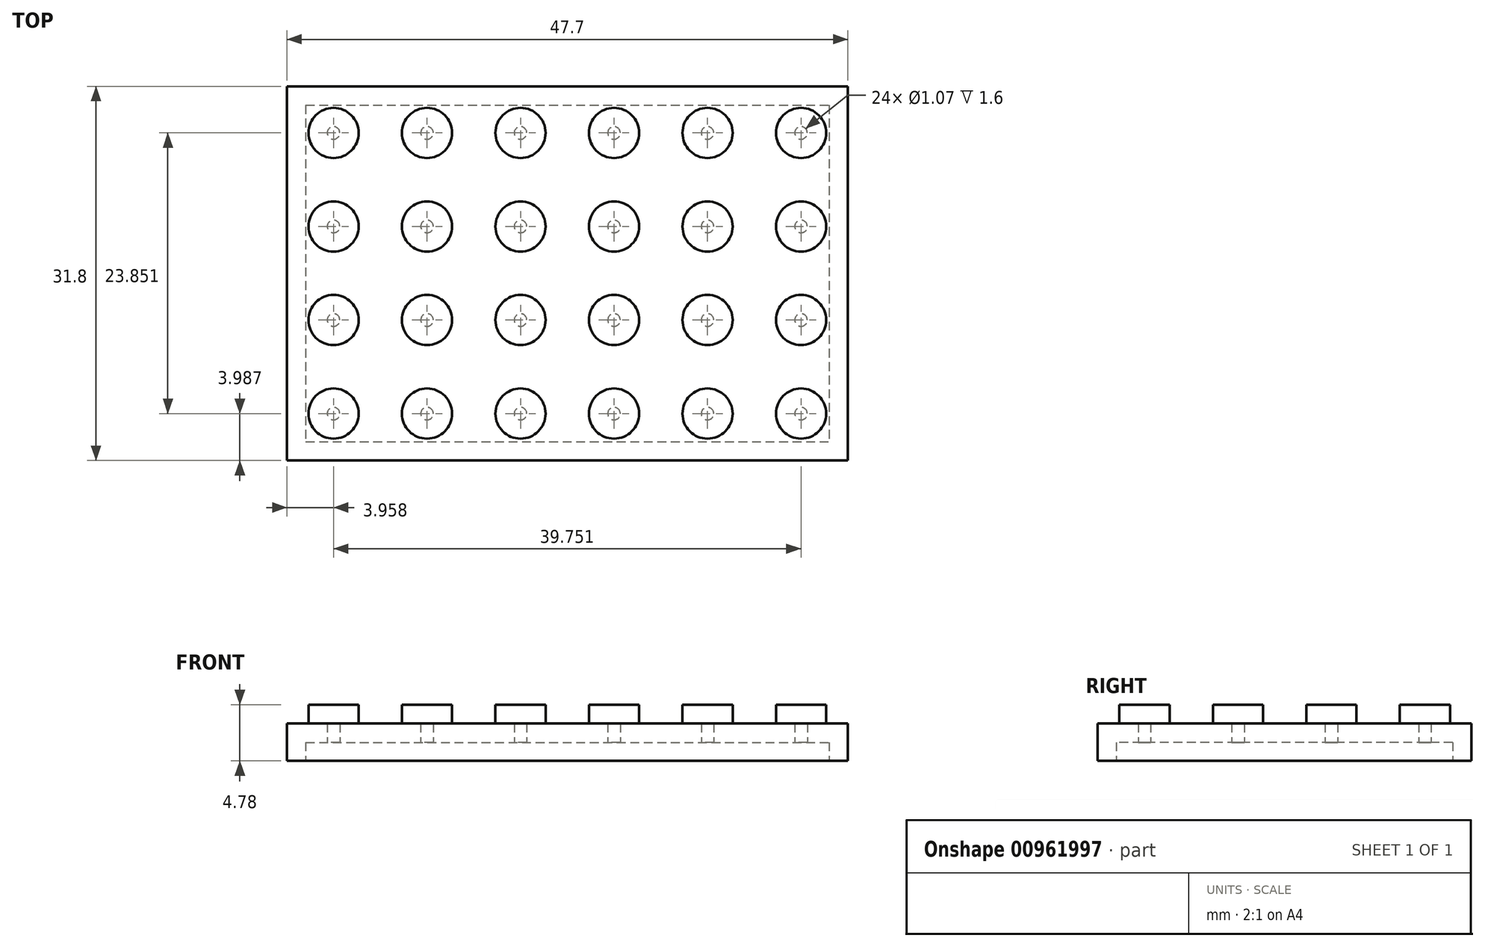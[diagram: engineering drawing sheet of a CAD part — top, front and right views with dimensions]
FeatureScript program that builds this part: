
annotation { "Feature Type Name" : "Feature", "Feature Type Description" : "" }
export const myFeature = defineFeature(function(context is Context, id is Id, definition is map)
    precondition{}
    {
        {
            var Q0;
            Q0=qCreatedBy(makeId("Top.planeOp"),FACE);
            var sketch = newSketch(context, id + "F0", { "sketchPlane" : qUnion([Q0])});
            skLineSegment(sketch, "E0.bottom", {"start": v(-28.22, 24.55) * mm, "end": v(19.48, 24.55) * mm});
            skLineSegment(sketch, "E0.top", {"start": v(-28.22, -7.25) * mm, "end": v(19.48, -7.25) * mm});
            skLineSegment(sketch, "E0.left", {"start": v(-28.22, 24.55) * mm, "end": v(-28.22, -7.25) * mm});
            skLineSegment(sketch, "E0.right", {"start": v(19.48, 24.55) * mm, "end": v(19.48, -7.25) * mm});
            skCircle(sketch, "E1", {"center": v(-24.26, 20.59) * mm, "radius": 2.13 * mm});
            skCircle(sketch, "E2.0.1.0", {"center": v(-24.26, 12.64) * mm, "radius": 2.13 * mm});
            skCircle(sketch, "E2.0.2.0", {"center": v(-24.26, 4.69) * mm, "radius": 2.13 * mm});
            skCircle(sketch, "E2.0.3.0", {"center": v(-24.26, -3.26) * mm, "radius": 2.13 * mm});
            skCircle(sketch, "E2.1.0.0", {"center": v(-16.31, 20.59) * mm, "radius": 2.13 * mm});
            skCircle(sketch, "E2.1.1.0", {"center": v(-16.31, 12.64) * mm, "radius": 2.13 * mm});
            skCircle(sketch, "E2.1.2.0", {"center": v(-16.31, 4.69) * mm, "radius": 2.13 * mm});
            skCircle(sketch, "E2.1.3.0", {"center": v(-16.31, -3.26) * mm, "radius": 2.13 * mm});
            skCircle(sketch, "E2.2.0.0", {"center": v(-8.36, 20.59) * mm, "radius": 2.13 * mm});
            skCircle(sketch, "E2.2.1.0", {"center": v(-8.36, 12.64) * mm, "radius": 2.13 * mm});
            skCircle(sketch, "E2.2.2.0", {"center": v(-8.36, 4.69) * mm, "radius": 2.13 * mm});
            skCircle(sketch, "E2.2.3.0", {"center": v(-8.36, -3.26) * mm, "radius": 2.13 * mm});
            skCircle(sketch, "E2.3.0.0", {"center": v(-0.41, 20.59) * mm, "radius": 2.13 * mm});
            skCircle(sketch, "E2.3.1.0", {"center": v(-0.41, 12.64) * mm, "radius": 2.13 * mm});
            skCircle(sketch, "E2.3.2.0", {"center": v(-0.41, 4.69) * mm, "radius": 2.13 * mm});
            skCircle(sketch, "E2.3.3.0", {"center": v(-0.41, -3.26) * mm, "radius": 2.13 * mm});
            skCircle(sketch, "E2.4.0.0", {"center": v(7.54, 20.59) * mm, "radius": 2.13 * mm});
            skCircle(sketch, "E2.4.1.0", {"center": v(7.54, 12.64) * mm, "radius": 2.13 * mm});
            skCircle(sketch, "E2.4.2.0", {"center": v(7.54, 4.69) * mm, "radius": 2.13 * mm});
            skCircle(sketch, "E2.4.3.0", {"center": v(7.54, -3.26) * mm, "radius": 2.13 * mm});
            skCircle(sketch, "E2.5.0.0", {"center": v(15.49, 20.59) * mm, "radius": 2.13 * mm});
            skCircle(sketch, "E2.5.1.0", {"center": v(15.49, 12.64) * mm, "radius": 2.13 * mm});
            skCircle(sketch, "E2.5.2.0", {"center": v(15.49, 4.69) * mm, "radius": 2.13 * mm});
            skCircle(sketch, "E2.5.3.0", {"center": v(15.49, -3.26) * mm, "radius": 2.13 * mm});
            skLineSegment(sketch, "E2.direction1", {"start": v(-24.26, 20.59) * mm, "end": v(-16.31, 20.59) * mm, "construction": true});
            skLineSegment(sketch, "E2.direction2", {"start": v(-24.26, 20.59) * mm, "end": v(-24.26, 12.64) * mm, "construction": true});
            skSolve(sketch);
        }
        {
            var Q0;
            Q0=makeQuery(id+"F0.imprint","IMPRINT",FACE,{"disambiguationData":[TD([[makeQuery(id+"F0.imprint","IMPRINT",EDGE,{"derivedFrom":sQuery(id+"F0.wireOp",EDGE,"E0.bottom")}),-1.0]])]});
            extrude(context, id + "F1", {"entities" : qUnion([Q0]), "depth" : 3.17 * mm, "offsetDistance" : 25.4 * mm});
        }
        {
            var Q0;
            Q0=makeQuery(id+"F0.imprint","IMPRINT",FACE,{"disambiguationData":[TD([[makeQuery(id+"F0.imprint","IMPRINT",EDGE,{"derivedFrom":sQuery(id+"F0.wireOp",EDGE,"E1")}),1.0]])]});
            var Q1;
            Q1=makeQuery(id+"F0.imprint","IMPRINT",FACE,{"disambiguationData":[TD([[makeQuery(id+"F0.imprint","IMPRINT",EDGE,{"derivedFrom":sQuery(id+"F0.wireOp",EDGE,"E2.1.0.0")}),1.0]])]});
            var Q2;
            Q2=makeQuery(id+"F0.imprint","IMPRINT",FACE,{"disambiguationData":[TD([[makeQuery(id+"F0.imprint","IMPRINT",EDGE,{"derivedFrom":sQuery(id+"F0.wireOp",EDGE,"E2.2.0.0")}),1.0]])]});
            var Q3;
            Q3=makeQuery(id+"F0.imprint","IMPRINT",FACE,{"disambiguationData":[TD([[makeQuery(id+"F0.imprint","IMPRINT",EDGE,{"derivedFrom":sQuery(id+"F0.wireOp",EDGE,"E2.3.0.0")}),1.0]])]});
            var Q4;
            Q4=makeQuery(id+"F0.imprint","IMPRINT",FACE,{"disambiguationData":[TD([[makeQuery(id+"F0.imprint","IMPRINT",EDGE,{"derivedFrom":sQuery(id+"F0.wireOp",EDGE,"E2.4.0.0")}),1.0]])]});
            var Q5;
            Q5=makeQuery(id+"F0.imprint","IMPRINT",FACE,{"disambiguationData":[TD([[makeQuery(id+"F0.imprint","IMPRINT",EDGE,{"derivedFrom":sQuery(id+"F0.wireOp",EDGE,"E2.5.0.0")}),1.0]])]});
            var Q6;
            Q6=makeQuery(id+"F0.imprint","IMPRINT",FACE,{"disambiguationData":[TD([[makeQuery(id+"F0.imprint","IMPRINT",EDGE,{"derivedFrom":sQuery(id+"F0.wireOp",EDGE,"E2.5.1.0")}),1.0]])]});
            var Q7;
            Q7=makeQuery(id+"F0.imprint","IMPRINT",FACE,{"disambiguationData":[TD([[makeQuery(id+"F0.imprint","IMPRINT",EDGE,{"derivedFrom":sQuery(id+"F0.wireOp",EDGE,"E2.4.1.0")}),1.0]])]});
            var Q8;
            Q8=makeQuery(id+"F0.imprint","IMPRINT",FACE,{"disambiguationData":[TD([[makeQuery(id+"F0.imprint","IMPRINT",EDGE,{"derivedFrom":sQuery(id+"F0.wireOp",EDGE,"E2.3.1.0")}),1.0]])]});
            var Q9;
            Q9=makeQuery(id+"F0.imprint","IMPRINT",FACE,{"disambiguationData":[TD([[makeQuery(id+"F0.imprint","IMPRINT",EDGE,{"derivedFrom":sQuery(id+"F0.wireOp",EDGE,"E2.2.1.0")}),1.0]])]});
            var Q10;
            Q10=makeQuery(id+"F0.imprint","IMPRINT",FACE,{"disambiguationData":[TD([[makeQuery(id+"F0.imprint","IMPRINT",EDGE,{"derivedFrom":sQuery(id+"F0.wireOp",EDGE,"E2.1.1.0")}),1.0]])]});
            var Q11;
            Q11=makeQuery(id+"F0.imprint","IMPRINT",FACE,{"disambiguationData":[TD([[makeQuery(id+"F0.imprint","IMPRINT",EDGE,{"derivedFrom":sQuery(id+"F0.wireOp",EDGE,"E2.0.1.0")}),1.0]])]});
            var Q12;
            Q12=makeQuery(id+"F0.imprint","IMPRINT",FACE,{"disambiguationData":[TD([[makeQuery(id+"F0.imprint","IMPRINT",EDGE,{"derivedFrom":sQuery(id+"F0.wireOp",EDGE,"E2.0.2.0")}),1.0]])]});
            var Q13;
            Q13=makeQuery(id+"F0.imprint","IMPRINT",FACE,{"disambiguationData":[TD([[makeQuery(id+"F0.imprint","IMPRINT",EDGE,{"derivedFrom":sQuery(id+"F0.wireOp",EDGE,"E2.1.2.0")}),1.0]])]});
            var Q14;
            Q14=makeQuery(id+"F0.imprint","IMPRINT",FACE,{"disambiguationData":[TD([[makeQuery(id+"F0.imprint","IMPRINT",EDGE,{"derivedFrom":sQuery(id+"F0.wireOp",EDGE,"E2.2.2.0")}),1.0]])]});
            var Q15;
            Q15=makeQuery(id+"F0.imprint","IMPRINT",FACE,{"disambiguationData":[TD([[makeQuery(id+"F0.imprint","IMPRINT",EDGE,{"derivedFrom":sQuery(id+"F0.wireOp",EDGE,"E2.3.2.0")}),1.0]])]});
            var Q16;
            Q16=makeQuery(id+"F0.imprint","IMPRINT",FACE,{"disambiguationData":[TD([[makeQuery(id+"F0.imprint","IMPRINT",EDGE,{"derivedFrom":sQuery(id+"F0.wireOp",EDGE,"E2.4.2.0")}),1.0]])]});
            var Q17;
            Q17=makeQuery(id+"F0.imprint","IMPRINT",FACE,{"disambiguationData":[TD([[makeQuery(id+"F0.imprint","IMPRINT",EDGE,{"derivedFrom":sQuery(id+"F0.wireOp",EDGE,"E2.5.2.0")}),1.0]])]});
            var Q18;
            Q18=makeQuery(id+"F0.imprint","IMPRINT",FACE,{"disambiguationData":[TD([[makeQuery(id+"F0.imprint","IMPRINT",EDGE,{"derivedFrom":sQuery(id+"F0.wireOp",EDGE,"E2.5.3.0")}),1.0]])]});
            var Q19;
            Q19=makeQuery(id+"F0.imprint","IMPRINT",FACE,{"disambiguationData":[TD([[makeQuery(id+"F0.imprint","IMPRINT",EDGE,{"derivedFrom":sQuery(id+"F0.wireOp",EDGE,"E2.4.3.0")}),1.0]])]});
            var Q20;
            Q20=makeQuery(id+"F0.imprint","IMPRINT",FACE,{"disambiguationData":[TD([[makeQuery(id+"F0.imprint","IMPRINT",EDGE,{"derivedFrom":sQuery(id+"F0.wireOp",EDGE,"E2.3.3.0")}),1.0]])]});
            var Q21;
            Q21=makeQuery(id+"F0.imprint","IMPRINT",FACE,{"disambiguationData":[TD([[makeQuery(id+"F0.imprint","IMPRINT",EDGE,{"derivedFrom":sQuery(id+"F0.wireOp",EDGE,"E2.2.3.0")}),1.0]])]});
            var Q22;
            Q22=makeQuery(id+"F0.imprint","IMPRINT",FACE,{"disambiguationData":[TD([[makeQuery(id+"F0.imprint","IMPRINT",EDGE,{"derivedFrom":sQuery(id+"F0.wireOp",EDGE,"E2.1.3.0")}),1.0]])]});
            var Q23;
            Q23=makeQuery(id+"F0.imprint","IMPRINT",FACE,{"disambiguationData":[TD([[makeQuery(id+"F0.imprint","IMPRINT",EDGE,{"derivedFrom":sQuery(id+"F0.wireOp",EDGE,"E2.0.3.0")}),1.0]])]});
            extrude(context, id + "F2", {"entities" : qUnion([Q0, Q1, Q2, Q3, Q4, Q5, Q6, Q7, Q8, Q9, Q10, Q11, Q12, Q13, Q14, Q15, Q16, Q17, Q18, Q19, Q20, Q21, Q22, Q23]), "operationType" : NewBodyOperationType.ADD, "depth" : 4.78 * mm, "offsetDistance" : 25.4 * mm});
        }
        {
            var Q0;
            {var subQ0=sQuery(id+"F0.wireOp",EDGE,"E2.5.3.0");var subQ1=sQuery(id+"F0.wireOp",EDGE,"E2.5.2.0");var subQ2=sQuery(id+"F0.wireOp",EDGE,"E2.5.1.0");var subQ3=sQuery(id+"F0.wireOp",EDGE,"E2.5.0.0");var subQ4=sQuery(id+"F0.wireOp",EDGE,"E2.4.3.0");var subQ5=sQuery(id+"F0.wireOp",EDGE,"E2.4.2.0");var subQ6=sQuery(id+"F0.wireOp",EDGE,"E2.4.1.0");var subQ7=sQuery(id+"F0.wireOp",EDGE,"E2.4.0.0");var subQ8=sQuery(id+"F0.wireOp",EDGE,"E2.3.3.0");var subQ9=sQuery(id+"F0.wireOp",EDGE,"E2.3.2.0");var subQ10=sQuery(id+"F0.wireOp",EDGE,"E2.3.1.0");var subQ11=sQuery(id+"F0.wireOp",EDGE,"E2.3.0.0");var subQ12=sQuery(id+"F0.wireOp",EDGE,"E2.2.3.0");var subQ13=sQuery(id+"F0.wireOp",EDGE,"E2.2.2.0");var subQ14=sQuery(id+"F0.wireOp",EDGE,"E2.2.1.0");var subQ15=sQuery(id+"F0.wireOp",EDGE,"E2.2.0.0");var subQ16=sQuery(id+"F0.wireOp",EDGE,"E2.1.3.0");var subQ17=sQuery(id+"F0.wireOp",EDGE,"E2.1.2.0");var subQ18=sQuery(id+"F0.wireOp",EDGE,"E2.1.1.0");var subQ19=sQuery(id+"F0.wireOp",EDGE,"E2.1.0.0");var subQ20=sQuery(id+"F0.wireOp",EDGE,"E2.0.3.0");var subQ21=sQuery(id+"F0.wireOp",EDGE,"E2.0.2.0");var subQ22=sQuery(id+"F0.wireOp",EDGE,"E2.0.1.0");var subQ23=sQuery(id+"F0.wireOp",EDGE,"E1");Q0=makeQuery(id+"F2.boolean.opBoolean","MERGE",FACE,{"derivedFrom":[makeQuery(id+"F1.opExtrude","CAP_FACE",FACE,{"disambiguationData":[OSD([sQuery(id+"F0.wireOp",EDGE,"E0.bottom"),sQuery(id+"F0.wireOp",EDGE,"E0.top"),sQuery(id+"F0.wireOp",EDGE,"E0.left"),sQuery(id+"F0.wireOp",EDGE,"E0.right"),subQ23,subQ22,subQ21,subQ20,subQ19,subQ18,subQ17,subQ16,subQ15,subQ14,subQ13,subQ12,subQ11,subQ10,subQ9,subQ8,subQ7,subQ6,subQ5,subQ4,subQ3,subQ2,subQ1,subQ0])],"isStart":true}),makeQuery(id+"F2.opExtrude","CAP_FACE",FACE,{"disambiguationData":[OSD([subQ23])],"isStart":true}),makeQuery(id+"F2.opExtrude","CAP_FACE",FACE,{"disambiguationData":[OSD([subQ22])],"isStart":true}),makeQuery(id+"F2.opExtrude","CAP_FACE",FACE,{"disambiguationData":[OSD([subQ21])],"isStart":true}),makeQuery(id+"F2.opExtrude","CAP_FACE",FACE,{"disambiguationData":[OSD([subQ20])],"isStart":true}),makeQuery(id+"F2.opExtrude","CAP_FACE",FACE,{"disambiguationData":[OSD([subQ19])],"isStart":true}),makeQuery(id+"F2.opExtrude","CAP_FACE",FACE,{"disambiguationData":[OSD([subQ18])],"isStart":true}),makeQuery(id+"F2.opExtrude","CAP_FACE",FACE,{"disambiguationData":[OSD([subQ17])],"isStart":true}),makeQuery(id+"F2.opExtrude","CAP_FACE",FACE,{"disambiguationData":[OSD([subQ16])],"isStart":true}),makeQuery(id+"F2.opExtrude","CAP_FACE",FACE,{"disambiguationData":[OSD([subQ15])],"isStart":true}),makeQuery(id+"F2.opExtrude","CAP_FACE",FACE,{"disambiguationData":[OSD([subQ14])],"isStart":true}),makeQuery(id+"F2.opExtrude","CAP_FACE",FACE,{"disambiguationData":[OSD([subQ13])],"isStart":true}),makeQuery(id+"F2.opExtrude","CAP_FACE",FACE,{"disambiguationData":[OSD([subQ12])],"isStart":true}),makeQuery(id+"F2.opExtrude","CAP_FACE",FACE,{"disambiguationData":[OSD([subQ11])],"isStart":true}),makeQuery(id+"F2.opExtrude","CAP_FACE",FACE,{"disambiguationData":[OSD([subQ10])],"isStart":true}),makeQuery(id+"F2.opExtrude","CAP_FACE",FACE,{"disambiguationData":[OSD([subQ9])],"isStart":true}),makeQuery(id+"F2.opExtrude","CAP_FACE",FACE,{"disambiguationData":[OSD([subQ8])],"isStart":true}),makeQuery(id+"F2.opExtrude","CAP_FACE",FACE,{"disambiguationData":[OSD([subQ7])],"isStart":true}),makeQuery(id+"F2.opExtrude","CAP_FACE",FACE,{"disambiguationData":[OSD([subQ6])],"isStart":true}),makeQuery(id+"F2.opExtrude","CAP_FACE",FACE,{"disambiguationData":[OSD([subQ5])],"isStart":true}),makeQuery(id+"F2.opExtrude","CAP_FACE",FACE,{"disambiguationData":[OSD([subQ4])],"isStart":true}),makeQuery(id+"F2.opExtrude","CAP_FACE",FACE,{"disambiguationData":[OSD([subQ3])],"isStart":true}),makeQuery(id+"F2.opExtrude","CAP_FACE",FACE,{"disambiguationData":[OSD([subQ2])],"isStart":true}),makeQuery(id+"F2.opExtrude","CAP_FACE",FACE,{"disambiguationData":[OSD([subQ1])],"isStart":true}),makeQuery(id+"F2.opExtrude","CAP_FACE",FACE,{"disambiguationData":[OSD([subQ0])],"isStart":true})]});}
            shell(context, id + "F3", {"entities" : qUnion([Q0]), "thickness" : 1.6 * mm});
        }
    });
